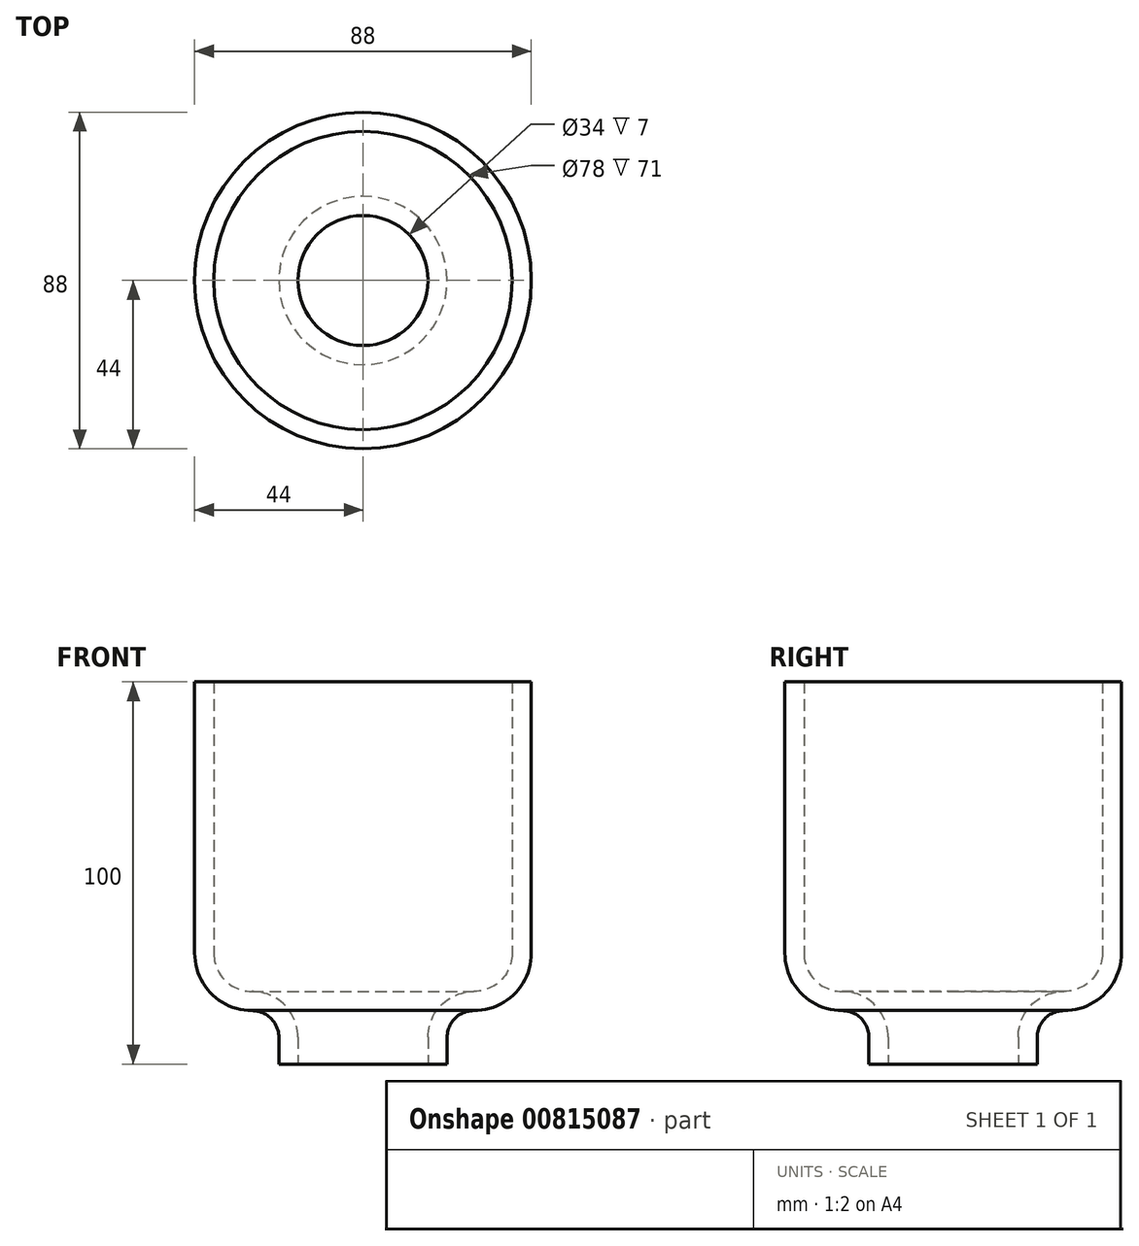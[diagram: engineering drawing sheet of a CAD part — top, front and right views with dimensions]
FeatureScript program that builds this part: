
annotation { "Feature Type Name" : "Feature", "Feature Type Description" : "" }
export const myFeature = defineFeature(function(context is Context, id is Id, definition is map)
    precondition{}
    {
        {
            var Q0;
            Q0=qCreatedBy(makeId("Front.planeOp"),FACE);
            var sketch = newSketch(context, id + "F0", { "sketchPlane" : qUnion([Q0])});
            skLineSegment(sketch, "E0", {"start": v(0, 0) * mm, "end": v(0, 7) * mm});
            skLineSegment(sketch, "E1", {"start": v(0, 0) * mm, "end": v(-5, 0) * mm});
            skLineSegment(sketch, "E2", {"start": v(-5, 0) * mm, "end": v(-5, 7) * mm});
            skLineSegment(sketch, "E3", {"start": v(-5, 7) * mm, "end": v(-12, 7) * mm});
            skArc(sketch, "E4", {"start": v(-5, 7) * mm, "mid": v(-7.05, 11.95) * mm, "end": v(-12, 14) * mm});
            skArc(sketch, "E5", {"start": v(0, 7) * mm, "mid": v(-1.11, 12.05) * mm, "end": v(-4.25, 16.16) * mm});
            skLineSegment(sketch, "E6", {"start": v(-12, 19) * mm, "end": v(-12, 29) * mm});
            skArc(sketch, "E7", {"start": v(-22, 29) * mm, "mid": v(-19.07, 21.93) * mm, "end": v(-12, 19) * mm});
            skArc(sketch, "E8", {"start": v(0, 7) * mm, "mid": v(-3.51, 15.49) * mm, "end": v(-12, 19) * mm});
            skLineSegment(sketch, "E9", {"start": v(-22, 29) * mm, "end": v(-22, 100) * mm});
            skLineSegment(sketch, "E10", {"start": v(-22, 100) * mm, "end": v(-27, 100) * mm});
            skLineSegment(sketch, "E11", {"start": v(-27, 100) * mm, "end": v(-27, 29) * mm});
            skArc(sketch, "E12.trimOffspring", {"start": v(-27, 29) * mm, "mid": v(-22.6, 18.4) * mm, "end": v(-12, 14) * mm});
            skLineSegment(sketch, "E13", {"start": v(17, 0) * mm, "end": v(17, 60.77) * mm});
            skSolve(sketch);
        }
        {
            var Q0;
            Q0 = qSketchRegion(id + "F0", true);
            var Q1;
            Q1=sQuery(id+"F0.wireOp",EDGE,"E13");
            revolve(context, id + "F1", {"surfaceOperationType" : NewSurfaceOperationType.NEW, "entities" : qUnion([Q0]), "axis" : qUnion([Q1]), "revolveType" : RevolveType.FULL});
        }
    });
